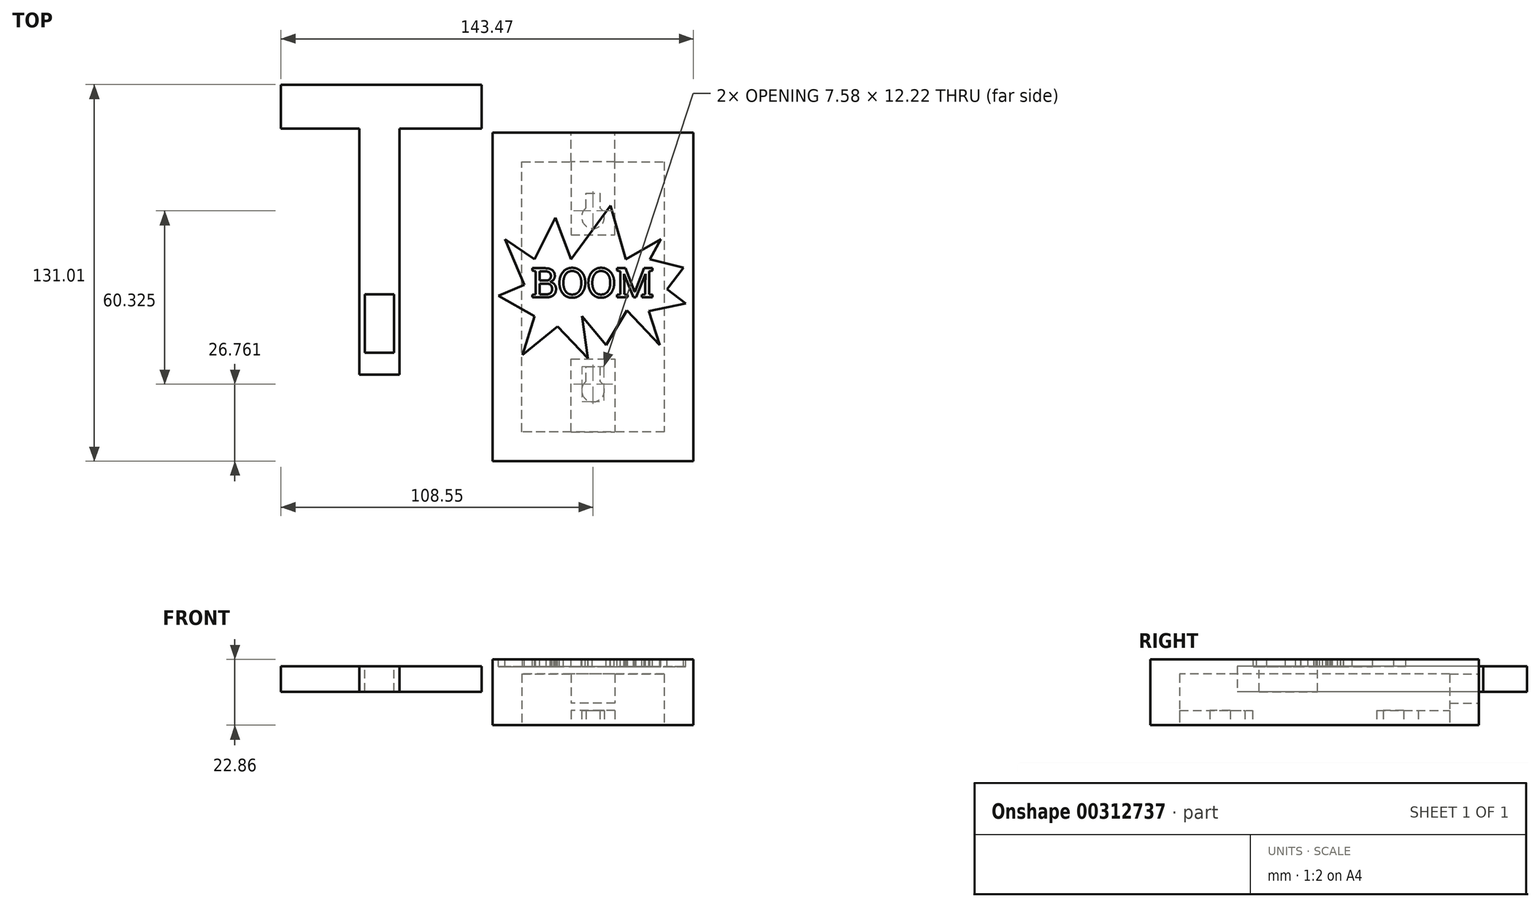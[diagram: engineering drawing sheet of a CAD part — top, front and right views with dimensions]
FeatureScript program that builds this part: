
annotation { "Feature Type Name" : "Feature", "Feature Type Description" : "" }
export const myFeature = defineFeature(function(context is Context, id is Id, definition is map)
    precondition{}
    {
        {
            var Q0;
            Q0=qCreatedBy(makeId("Top.planeOp"),FACE);
            var sketch = newSketch(context, id + "F0", { "sketchPlane" : qUnion([Q0])});
            skCircle(sketch, "E0", {"center": v(0, 34.46) * mm, "radius": 3.97 * mm});
            skCircle(sketch, "E1", {"center": v(0, -25.87) * mm, "radius": 3.97 * mm});
            skLineSegment(sketch, "E2", {"start": v(-34.92, 63.81) * mm, "end": v(34.93, 63.81) * mm});
            skLineSegment(sketch, "E3", {"start": v(34.93, 63.81) * mm, "end": v(34.93, -50.49) * mm});
            skLineSegment(sketch, "E4", {"start": v(34.93, -50.49) * mm, "end": v(-34.92, -50.49) * mm});
            skLineSegment(sketch, "E5", {"start": v(-34.92, -50.49) * mm, "end": v(-34.92, 63.81) * mm});
            skLineSegment(sketch, "E6", {"start": v(-24.76, -40.33) * mm, "end": v(-24.76, 53.65) * mm});
            skLineSegment(sketch, "E7", {"start": v(-24.76, 53.65) * mm, "end": v(24.77, 53.65) * mm});
            skLineSegment(sketch, "E8", {"start": v(24.77, 53.65) * mm, "end": v(24.77, -40.33) * mm});
            skLineSegment(sketch, "E9", {"start": v(24.77, -40.33) * mm, "end": v(-24.76, -40.33) * mm});
            skLineSegment(sketch, "E10", {"start": v(-2.39, 37.63) * mm, "end": v(-2.39, 42.7) * mm});
            skLineSegment(sketch, "E11", {"start": v(2.39, 42.7) * mm, "end": v(2.39, 37.63) * mm});
            skLineSegment(sketch, "E12", {"start": v(-2.39, 42.7) * mm, "end": v(0, 42.7) * mm});
            skLineSegment(sketch, "E13", {"start": v(0, 42.7) * mm, "end": v(2.39, 42.7) * mm});
            skLineSegment(sketch, "E14", {"start": v(-2.39, -22.7) * mm, "end": v(-2.39, -17.62) * mm});
            skLineSegment(sketch, "E15", {"start": v(-2.39, -17.62) * mm, "end": v(0, -17.62) * mm});
            skLineSegment(sketch, "E16", {"start": v(0, -17.62) * mm, "end": v(2.39, -17.62) * mm});
            skLineSegment(sketch, "E17", {"start": v(2.39, -17.62) * mm, "end": v(2.39, -22.7) * mm});
            skLineSegment(sketch, "E18", {"start": v(-7.62, 53.65) * mm, "end": v(-7.62, 28.25) * mm});
            skLineSegment(sketch, "E19", {"start": v(7.62, 28.25) * mm, "end": v(7.62, 53.65) * mm});
            skLineSegment(sketch, "E20", {"start": v(-7.62, 28.25) * mm, "end": v(0, 28.25) * mm});
            skLineSegment(sketch, "E21", {"start": v(0, 28.25) * mm, "end": v(7.62, 28.25) * mm});
            skLineSegment(sketch, "E22", {"start": v(-7.62, -40.33) * mm, "end": v(-7.62, -14.93) * mm});
            skLineSegment(sketch, "E23", {"start": v(-7.62, -14.93) * mm, "end": v(0, -14.93) * mm});
            skLineSegment(sketch, "E24", {"start": v(0, -14.93) * mm, "end": v(7.62, -14.93) * mm});
            skLineSegment(sketch, "E25", {"start": v(7.62, -14.93) * mm, "end": v(7.62, -40.33) * mm});
            skSolve(sketch);
        }
        {
            var Q0;
            Q0=makeQuery(id+"F0.imprint","IMPRINT",FACE,{"disambiguationData":[TD([[makeQuery(id+"F0.imprint","IMPRINT",EDGE,{"derivedFrom":sQuery(id+"F0.wireOp",EDGE,"E2")}),-1.0]])]});
            var Q1;
            {var subQ0=sQuery(id+"F0.wireOp",EDGE,"E14");Q1=makeQuery(id+"F0.imprint","IMPRINT",FACE,{"disambiguationData":[TD([[makeQuery(id+"F0.imprint","IMPRINT",EDGE,{"derivedFrom":subQ0}),1.0]])]});}
            var Q2;
            {var subQ4=sQuery(id+"F0.wireOp",EDGE,"E10");Q2=makeQuery(id+"F0.imprint","IMPRINT",FACE,{"disambiguationData":[TD([[makeQuery(id+"F0.imprint","IMPRINT",EDGE,{"derivedFrom":subQ4}),1.0]])]});}
            extrude(context, id + "F1", {"entities" : qUnion([Q0, Q1, Q2]), "depth" : 5.08 * mm});
        }
        {
            var Q0;
            Q0=makeQuery(id+"F0.imprint","IMPRINT",FACE,{"disambiguationData":[TD([[makeQuery(id+"F0.imprint","IMPRINT",EDGE,{"derivedFrom":sQuery(id+"F0.wireOp",EDGE,"E2")}),-1.0]])]});
            extrude(context, id + "F2", {"entities" : qUnion([Q0]), "operationType" : NewBodyOperationType.ADD, "depth" : 10.16 * mm});
        }
        {
            var Q0;
            Q0=makeQuery(id+"F2.opExtrude","CAP_FACE",FACE,{"disambiguationData":[OSD([sQuery(id+"F0.wireOp",EDGE,"E2"),sQuery(id+"F0.wireOp",EDGE,"E3"),sQuery(id+"F0.wireOp",EDGE,"E4"),sQuery(id+"F0.wireOp",EDGE,"E5"),sQuery(id+"F0.wireOp",EDGE,"E6"),sQuery(id+"F0.wireOp",EDGE,"E7"),sQuery(id+"F0.wireOp",EDGE,"E8"),sQuery(id+"F0.wireOp",EDGE,"E9")])],"isStart":false});
            var sketch = newSketch(context, id + "F3", { "sketchPlane" : qUnion([Q0])});
            skLineSegment(sketch, "E26.0", {"start": v(-34.92, 63.81) * mm, "end": v(34.93, 63.81) * mm});
            skLineSegment(sketch, "E26.1", {"start": v(-34.92, -50.49) * mm, "end": v(-34.92, 63.81) * mm});
            skLineSegment(sketch, "E26.2", {"start": v(34.93, -50.49) * mm, "end": v(-34.92, -50.49) * mm});
            skLineSegment(sketch, "E26.3", {"start": v(34.93, 63.81) * mm, "end": v(34.93, -50.49) * mm});
            skSolve(sketch);
        }
        {
            var Q0;
            Q0=makeQuery(id+"F3.imprint","IMPRINT",FACE,{"disambiguationData":[TD([[makeQuery(id+"F3.imprint","IMPRINT",EDGE,{"derivedFrom":sQuery(id+"F3.wireOp",EDGE,"E26.0")}),-1.0]])]});
            var Q1;
            Q1=makeQuery(id+"F3.imprint","IMPRINT",FACE,{"disambiguationData":[TD([[makeQuery(id+"F3.imprint","IMPRINT",EDGE,{"derivedFrom":makeQuery(id+"F2.opExtrude","CAP_EDGE",EDGE,{"disambiguationData":[OSD([sQuery(id+"F0.wireOp",EDGE,"E6")])],"isStart":false})}),-1.0]])]});
            extrude(context, id + "F4", {"entities" : qUnion([Q0, Q1]), "operationType" : NewBodyOperationType.ADD, "depth" : 12.7 * mm});
        }
        {
            var Q0;
            Q0=makeQuery(id+"F3.imprint","IMPRINT",FACE,{"disambiguationData":[TD([[makeQuery(id+"F3.imprint","IMPRINT",EDGE,{"derivedFrom":sQuery(id+"F3.wireOp",EDGE,"E26.0")}),-1.0]])]});
            var sketch = newSketch(context, id + "F5", { "sketchPlane" : qUnion([Q0])});
            skLineSegment(sketch, "E27.0", {"start": v(-24.76, 53.65) * mm, "end": v(24.77, 53.65) * mm});
            skLineSegment(sketch, "E27.1", {"start": v(-24.76, -40.33) * mm, "end": v(-24.76, 53.65) * mm});
            skLineSegment(sketch, "E27.2", {"start": v(24.77, -40.33) * mm, "end": v(-24.76, -40.33) * mm});
            skLineSegment(sketch, "E27.3", {"start": v(24.77, 53.65) * mm, "end": v(24.77, -40.33) * mm});
            skSolve(sketch);
        }
        {
            var Q0;
            Q0 = qSketchRegion(id + "F5", true);
            extrude(context, id + "F6", {"entities" : qUnion([Q0]), "operationType" : NewBodyOperationType.REMOVE, "depth" : 7.62 * mm});
        }
        {
            var Q0;
            {var subQ0=sQuery(id+"F0.wireOp",EDGE,"E2");Q0=makeQuery(id+"F4.boolean.opBoolean","MERGE",FACE,{"derivedFrom":[makeQuery(id+"F2.boolean.opBoolean","MERGE",FACE,{"derivedFrom":[makeQuery(id+"F1.opExtrude","SWEPT_FACE",FACE,{"disambiguationData":[OSD([subQ0])]}),makeQuery(id+"F2.opExtrude","SWEPT_FACE",FACE,{"disambiguationData":[OSD([subQ0])]})]}),makeQuery(id+"F4.opExtrude","SWEPT_FACE",FACE,{"disambiguationData":[OSD([sQuery(id+"F3.wireOp",EDGE,"E26.0")])]})]});}
            var sketch = newSketch(context, id + "F7", { "sketchPlane" : qUnion([Q0])});
            skLineSegment(sketch, "E28.0", {"start": v(34.92, 22.86) * mm, "end": v(-34.93, 22.86) * mm});
            skLineSegment(sketch, "E28.1", {"start": v(-34.93, 22.86) * mm, "end": v(-34.93, 0) * mm});
            skLineSegment(sketch, "E28.2", {"start": v(-34.93, 0) * mm, "end": v(34.92, 0) * mm});
            skLineSegment(sketch, "E28.3", {"start": v(34.92, 22.86) * mm, "end": v(34.92, 0) * mm});
            skLineSegment(sketch, "E29.bottom", {"start": v(-7.62, 17.78) * mm, "end": v(7.62, 17.78) * mm});
            skLineSegment(sketch, "E29.top", {"start": v(-7.62, 7.62) * mm, "end": v(7.62, 7.62) * mm});
            skLineSegment(sketch, "E29.left", {"start": v(-7.62, 17.78) * mm, "end": v(-7.62, 7.62) * mm});
            skLineSegment(sketch, "E29.right", {"start": v(7.62, 17.78) * mm, "end": v(7.62, 7.62) * mm});
            skSolve(sketch);
        }
        {
            var Q0;
            Q0=makeQuery(id+"F7.imprint","IMPRINT",FACE,{"disambiguationData":[TD([[makeQuery(id+"F7.imprint","IMPRINT",EDGE,{"derivedFrom":sQuery(id+"F7.wireOp",EDGE,"E29.bottom")}),-1.0]])]});
            extrude(context, id + "F8", {"entities" : qUnion([Q0]), "operationType" : NewBodyOperationType.REMOVE, "oppositeDirection" : true, "depth" : 25.4 * mm});
        }
        {
            var Q0;
            Q0=makeQuery(id+"F4.opExtrude","CAP_FACE",FACE,{"disambiguationData":[OSD([sQuery(id+"F3.wireOp",EDGE,"E26.0"),sQuery(id+"F3.wireOp",EDGE,"E26.1"),sQuery(id+"F3.wireOp",EDGE,"E26.2"),sQuery(id+"F3.wireOp",EDGE,"E26.3")])],"isStart":false});
            var sketch = newSketch(context, id + "F9", { "sketchPlane" : qUnion([Q0])});
            skText(sketch, "E30", { "text": "BOOM", "fontName": "RobotoSlab-Regular.ttf"});
            skPoint(sketch, "E31", {"position": v(21.59, 11.64) * mm});
            skLineSegment(sketch, "E32", {"start": v(-12.28, -3.6) * mm, "end": v(-24.5, -13.53) * mm});
            skLineSegment(sketch, "E33", {"start": v(-24.5, -13.53) * mm, "end": v(-20.3, 0) * mm});
            skLineSegment(sketch, "E34", {"start": v(-20.3, 0) * mm, "end": v(-32.9, 7.1) * mm});
            skLineSegment(sketch, "E35", {"start": v(-32.9, 7.1) * mm, "end": v(-23.93, 10.91) * mm});
            skLineSegment(sketch, "E36", {"start": v(-23.93, 10.91) * mm, "end": v(-30.66, 26.73) * mm});
            skLineSegment(sketch, "E37", {"start": v(-30.66, 26.73) * mm, "end": v(-20.3, 19.7) * mm});
            skLineSegment(sketch, "E38", {"start": v(-20.3, 19.7) * mm, "end": v(-13.04, 34.2) * mm});
            skLineSegment(sketch, "E39", {"start": v(-13.04, 34.2) * mm, "end": v(-7.7, 19.7) * mm});
            skLineSegment(sketch, "E40", {"start": v(-7.7, 19.7) * mm, "end": v(6.05, 38.4) * mm});
            skLineSegment(sketch, "E41", {"start": v(6.05, 38.4) * mm, "end": v(11.4, 19.7) * mm});
            skLineSegment(sketch, "E42", {"start": v(11.4, 19.7) * mm, "end": v(23.62, 26.73) * mm});
            skLineSegment(sketch, "E43", {"start": v(23.62, 26.73) * mm, "end": v(19.8, 19.7) * mm});
            skLineSegment(sketch, "E44", {"start": v(19.8, 19.7) * mm, "end": v(31.45, 16.78) * mm});
            skLineSegment(sketch, "E45", {"start": v(31.45, 16.78) * mm, "end": v(25.72, 9.38) * mm});
            skLineSegment(sketch, "E46", {"start": v(25.72, 9.38) * mm, "end": v(32.25, 4.33) * mm});
            skLineSegment(sketch, "E47", {"start": v(32.25, 4.33) * mm, "end": v(19.42, 1.74) * mm});
            skLineSegment(sketch, "E48", {"start": v(19.42, 1.74) * mm, "end": v(23.24, -10.1) * mm});
            skLineSegment(sketch, "E49", {"start": v(23.24, -10.1) * mm, "end": v(11.78, 1.94) * mm});
            skLineSegment(sketch, "E50", {"start": v(11.78, 1.94) * mm, "end": v(4.52, -10.1) * mm});
            skLineSegment(sketch, "E51", {"start": v(4.52, -10.1) * mm, "end": v(-3.88, 0) * mm});
            skLineSegment(sketch, "E52", {"start": v(-3.88, 0) * mm, "end": v(-1.78, -14.68) * mm});
            skLineSegment(sketch, "E53", {"start": v(-1.78, -14.68) * mm, "end": v(-12.28, -3.6) * mm});
            const initialGuessF9  = {"E30": [-0.0216, 0.0065, 1, 0, 0.01027]};
            skSetInitialGuess(sketch, initialGuessF9);
            skSolve(sketch);
        }
        {
            var Q0;
            Q0 = qSketchRegion(id + "F9", true);
            extrude(context, id + "F10", {"entities" : qUnion([Q0]), "operationType" : NewBodyOperationType.REMOVE, "oppositeDirection" : true, "depth" : 2.54 * mm});
        }
        {
            var Q0;
            Q0=makeQuery(id+"F9.imprint","IMPRINT",FACE,{"disambiguationData":[TD([[makeQuery(id+"F9.imprint","IMPRINT",EDGE,{"derivedFrom":sQuery(id+"F9.wireOp",EDGE,"E30.sketch_text.stroke-40")}),1.0]])]});
            var Q1;
            Q1=makeQuery(id+"F9.imprint","IMPRINT",FACE,{"disambiguationData":[TD([[makeQuery(id+"F9.imprint","IMPRINT",EDGE,{"derivedFrom":sQuery(id+"F9.wireOp",EDGE,"E30.sketch_text.stroke-60")}),1.0]])]});
            var Q2;
            Q2=makeQuery(id+"F9.imprint","IMPRINT",FACE,{"disambiguationData":[TD([[makeQuery(id+"F9.imprint","IMPRINT",EDGE,{"derivedFrom":sQuery(id+"F9.wireOp",EDGE,"E30.sketch_text.stroke-23")}),1.0]])]});
            var Q3;
            Q3=makeQuery(id+"F9.imprint","IMPRINT",FACE,{"disambiguationData":[TD([[makeQuery(id+"F9.imprint","IMPRINT",EDGE,{"derivedFrom":sQuery(id+"F9.wireOp",EDGE,"E30.sketch_text.stroke-16")}),1.0]])]});
            extrude(context, id + "F11", {"entities" : qUnion([Q0, Q1, Q2, Q3]), "operationType" : NewBodyOperationType.REMOVE, "oppositeDirection" : true, "depth" : 2.54 * mm});
        }
        {
            var Q0;
            Q0=qCreatedBy(makeId("Front.planeOp"),FACE);
            var sketch = newSketch(context, id + "F12", { "sketchPlane" : qUnion([Q0])});
            skLineSegment(sketch, "E54.bottom", {"start": v(-67.27, 20.54) * mm, "end": v(-81.24, 20.54) * mm});
            skLineSegment(sketch, "E54.top", {"start": v(-67.27, 11.65) * mm, "end": v(-81.24, 11.65) * mm});
            skLineSegment(sketch, "E54.left", {"start": v(-67.27, 20.54) * mm, "end": v(-67.27, 11.65) * mm});
            skLineSegment(sketch, "E54.right", {"start": v(-81.24, 20.54) * mm, "end": v(-81.24, 11.65) * mm});
            skSolve(sketch);
        }
        {
            var Q0;
            Q0=makeQuery(id+"F12.imprint","IMPRINT",FACE,{"disambiguationData":[TD([[makeQuery(id+"F12.imprint","IMPRINT",EDGE,{"derivedFrom":sQuery(id+"F12.wireOp",EDGE,"E54.bottom")}),1.0]])]});
            extrude(context, id + "F13", {"entities" : qUnion([Q0]), "oppositeDirection" : true, "depth" : 65.28 * mm});
        }
        {
            var Q0;
            Q0=makeQuery(id+"F13.opExtrude","CAP_FACE",FACE,{"disambiguationData":[OSD([sQuery(id+"F12.wireOp",EDGE,"E54.bottom"),sQuery(id+"F12.wireOp",EDGE,"E54.top"),sQuery(id+"F12.wireOp",EDGE,"E54.left"),sQuery(id+"F12.wireOp",EDGE,"E54.right")])],"isStart":true});
            extrude(context, id + "F14", {"entities" : qUnion([Q0]), "operationType" : NewBodyOperationType.ADD, "depth" : 20.32 * mm});
        }
        {
            var Q0;
            {var subQ0=sQuery(id+"F12.wireOp",EDGE,"E54.bottom");Q0=makeQuery(id+"F14.boolean.opBoolean","MERGE",FACE,{"derivedFrom":[makeQuery(id+"F13.opExtrude","SWEPT_FACE",FACE,{"disambiguationData":[OSD([subQ0])]}),makeQuery(id+"F14.opExtrude","SWEPT_FACE",FACE,{"disambiguationData":[OSD([subQ0])]})]});}
            var sketch = newSketch(context, id + "F15", { "sketchPlane" : qUnion([Q0])});
            skLineSegment(sketch, "E55", {"start": v(-79.34, 7.62) * mm, "end": v(-79.34, -12.7) * mm});
            skLineSegment(sketch, "E56", {"start": v(-79.34, -12.7) * mm, "end": v(-69.18, -12.7) * mm});
            skLineSegment(sketch, "E57", {"start": v(-69.18, -12.7) * mm, "end": v(-69.18, 7.62) * mm});
            skLineSegment(sketch, "E58", {"start": v(-69.18, 7.62) * mm, "end": v(-79.34, 7.62) * mm});
            skLineSegment(sketch, "E59.0", {"start": v(-67.27, 65.28) * mm, "end": v(-81.24, 65.28) * mm});
            skSolve(sketch);
        }
        {
            var Q0;
            Q0=makeQuery(id+"F15.imprint","IMPRINT",FACE,{"disambiguationData":[TD([[makeQuery(id+"F15.imprint","IMPRINT",EDGE,{"derivedFrom":sQuery(id+"F15.wireOp",EDGE,"E55")}),1.0]])]});
            extrude(context, id + "F16", {"entities" : qUnion([Q0]), "operationType" : NewBodyOperationType.REMOVE, "oppositeDirection" : true, "depth" : 25.4 * mm});
        }
        {
            var Q0;
            Q0=makeQuery(id+"F13.opExtrude","CAP_FACE",FACE,{"disambiguationData":[OSD([sQuery(id+"F12.wireOp",EDGE,"E54.bottom"),sQuery(id+"F12.wireOp",EDGE,"E54.top"),sQuery(id+"F12.wireOp",EDGE,"E54.left"),sQuery(id+"F12.wireOp",EDGE,"E54.right")])],"isStart":false});
            var sketch = newSketch(context, id + "F17", { "sketchPlane" : qUnion([Q0])});
            skLineSegment(sketch, "E60", {"start": v(38.7, 20.54) * mm, "end": v(108.55, 20.54) * mm});
            skLineSegment(sketch, "E61", {"start": v(108.55, 20.54) * mm, "end": v(108.55, 11.65) * mm});
            skLineSegment(sketch, "E62", {"start": v(108.55, 11.65) * mm, "end": v(38.7, 11.65) * mm});
            skLineSegment(sketch, "E63", {"start": v(38.7, 11.65) * mm, "end": v(38.7, 20.54) * mm});
            skSolve(sketch);
        }
        {
            var Q0;
            {var subQ2=sQuery(id+"F17.wireOp",EDGE,"E63");Q0=makeQuery(id+"F17.imprint","IMPRINT",FACE,{"disambiguationData":[TD([[makeQuery(id+"F17.imprint","IMPRINT",EDGE,{"derivedFrom":subQ2}),-1.0]])]});}
            var Q1;
            {var subQ1=makeQuery(id+"F13.opExtrude","CAP_EDGE",EDGE,{"disambiguationData":[OSD([sQuery(id+"F12.wireOp",EDGE,"E54.left")])],"isStart":false});Q1=makeQuery(id+"F17.imprint","IMPRINT",FACE,{"disambiguationData":[TD([[makeQuery(id+"F17.imprint","IMPRINT",EDGE,{"derivedFrom":subQ1}),1.0]])]});}
            var Q2;
            {var subQ2=sQuery(id+"F17.wireOp",EDGE,"E61");Q2=makeQuery(id+"F17.imprint","IMPRINT",FACE,{"disambiguationData":[TD([[makeQuery(id+"F17.imprint","IMPRINT",EDGE,{"derivedFrom":subQ2}),-1.0]])]});}
            extrude(context, id + "F18", {"entities" : qUnion([Q0, Q1, Q2]), "operationType" : NewBodyOperationType.ADD, "depth" : 15.24 * mm});
        }
    });
